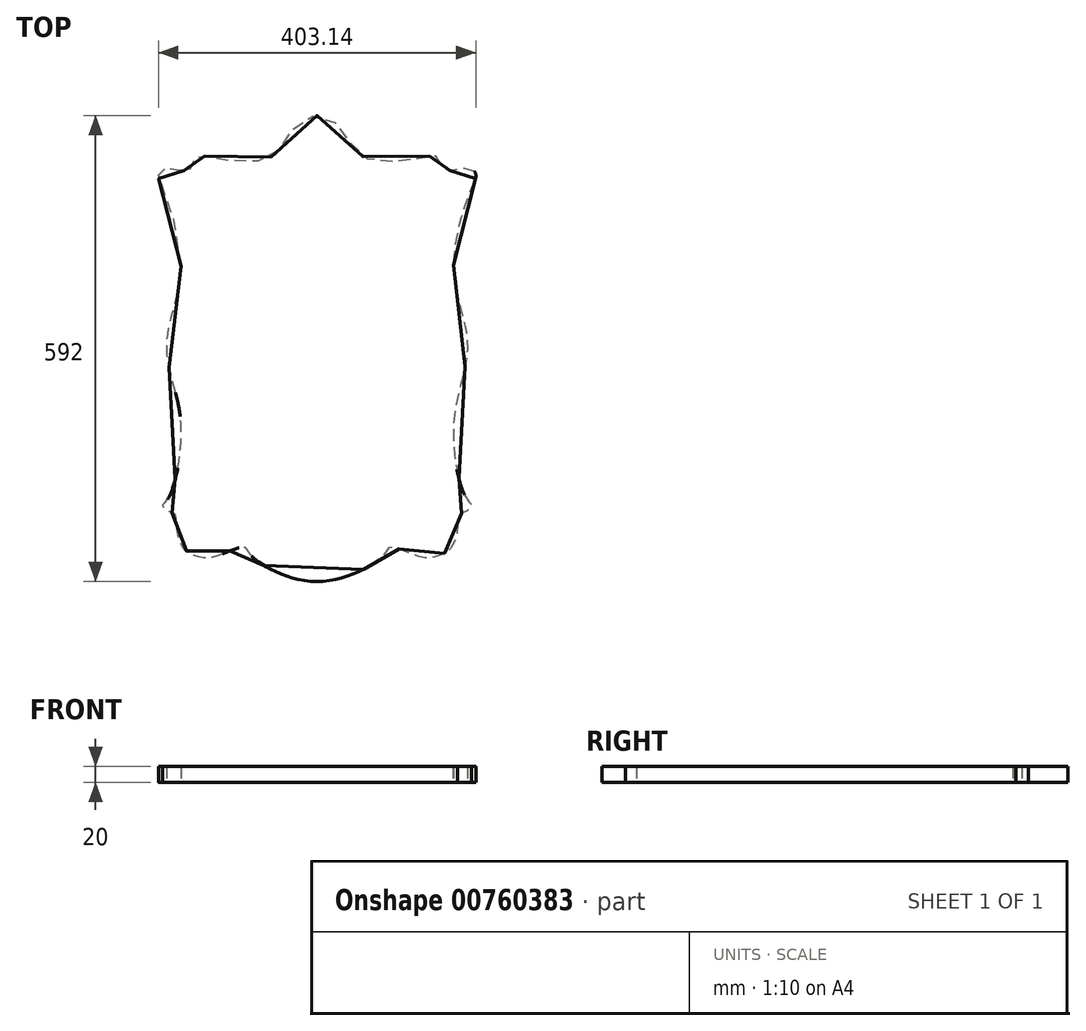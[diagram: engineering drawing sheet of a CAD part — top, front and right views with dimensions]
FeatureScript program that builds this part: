
annotation { "Feature Type Name" : "Feature", "Feature Type Description" : "" }
export const myFeature = defineFeature(function(context is Context, id is Id, definition is map)
    precondition{}
    {
        {
            var Q0;
            Q0=qCreatedBy(makeId("Top.planeOp"),FACE);
            var sketch = newSketch(context, id + "F0", { "sketchPlane" : qUnion([Q0])});
            skPoint(sketch, "E0", {"position": v(140, 240) * mm});
            skPoint(sketch, "E1", {"position": v(163, 223) * mm});
            skPoint(sketch, "E2", {"position": v(185, 225) * mm});
            skPoint(sketch, "E3", {"position": v(197, 202) * mm});
            skPoint(sketch, "E4", {"position": v(196, -202) * mm});
            skPoint(sketch, "E5", {"position": v(140, -270) * mm});
            skPoint(sketch, "E6", {"position": v(90, -258) * mm});
            skPoint(sketch, "E7", {"position": v(0, -300) * mm});
            skPoint(sketch, "E8", {"position": v(180, -216) * mm});
            skPoint(sketch, "E9", {"position": v(173, 101) * mm});
            skPoint(sketch, "E10", {"position": v(191, 0) * mm});
            skPoint(sketch, "E11", {"position": v(0, 292) * mm});
            skPoint(sketch, "E12", {"position": v(95, 234) * mm});
            skPoint(sketch, "E13", {"position": v(173, -101) * mm});
            skPoint(sketch, "E14", {"position": v(-158.4, 227.4) * mm});
            skPoint(sketch, "E15", {"position": v(-200.24, 220.68) * mm});
            skPoint(sketch, "E16", {"position": v(-169.15, 222.02) * mm});
            skPoint(sketch, "E17", {"position": v(-54.11, 242.56) * mm});
            skPoint(sketch, "E18", {"position": v(-31.45, 273.93) * mm});
            skPoint(sketch, "E19", {"position": v(-155, 238.03) * mm});
            skPoint(sketch, "E20", {"position": v(-194.35, 225.38) * mm});
            skPoint(sketch, "E21", {"position": v(-201.42, 213.06) * mm});
            skLineSegment(sketch, "E22", {"start": v(0, 292) * mm, "end": v(0, -300) * mm, "construction": true});
            skPoint(sketch, "E23.MirrorP", {"position": v(-95, 234) * mm});
            skPoint(sketch, "E24.MirrorP", {"position": v(-140, 240) * mm});
            skPoint(sketch, "E25.MirrorP", {"position": v(-163, 223) * mm});
            skPoint(sketch, "E26.MirrorP", {"position": v(-185, 225) * mm});
            skPoint(sketch, "E27.MirrorP", {"position": v(-197, 202) * mm});
            skPoint(sketch, "E28.MirrorP", {"position": v(-173, 101) * mm});
            skPoint(sketch, "E29.MirrorP", {"position": v(-191, 0) * mm});
            skPoint(sketch, "E30.MirrorP", {"position": v(-173, -101) * mm});
            skPoint(sketch, "E31.MirrorP", {"position": v(-196, -202) * mm});
            skPoint(sketch, "E32.MirrorP", {"position": v(-180, -216) * mm});
            skPoint(sketch, "E33.MirrorP", {"position": v(-140, -270) * mm});
            skPoint(sketch, "E34.MirrorP", {"position": v(-90, -258) * mm});
            skPoint(sketch, "E35", {"position": v(0, 0) * mm});
            skPoint(sketch, "E36", {"position": v(-190.7, -196.69) * mm});
            skPoint(sketch, "E37", {"position": v(-178.47, -230.66) * mm});
            skPoint(sketch, "E38", {"position": v(-190.7, -210) * mm});
            skPoint(sketch, "E39", {"position": v(-170.86, -255.98) * mm});
            skPoint(sketch, "E40", {"position": v(-123.63, -266.12) * mm});
            skPoint(sketch, "E41", {"position": v(-79, -271.56) * mm});
            skPoint(sketch, "E42", {"position": v(-87.69, -261.38) * mm});
            skPoint(sketch, "E43", {"position": v(-94.51, -256.16) * mm});
            skPoint(sketch, "E44", {"position": v(-155.65, -266.93) * mm});
            skPoint(sketch, "E45", {"position": v(-195.44, -204.34) * mm});
            skPoint(sketch, "E46.MirrorP", {"position": v(79, -271.56) * mm});
            skPoint(sketch, "E47.MirrorP", {"position": v(87.69, -261.38) * mm});
            skPoint(sketch, "E48.MirrorP", {"position": v(94.51, -256.16) * mm});
            skPoint(sketch, "E49.MirrorP", {"position": v(123.64, -266.11) * mm});
            skPoint(sketch, "E50.MirrorP", {"position": v(155.65, -266.93) * mm});
            skPoint(sketch, "E51.MirrorP", {"position": v(178.47, -230.66) * mm});
            skPoint(sketch, "E52.MirrorP", {"position": v(190.7, -210) * mm});
            skPoint(sketch, "E53.MirrorP", {"position": v(195.44, -204.34) * mm});
            skPoint(sketch, "E54.MirrorP", {"position": v(190.7, -196.69) * mm});
            skPoint(sketch, "E55.MirrorP", {"position": v(201.42, 213.06) * mm});
            skPoint(sketch, "E56.MirrorP", {"position": v(200.24, 220.68) * mm});
            skPoint(sketch, "E57.MirrorP", {"position": v(194.35, 225.38) * mm});
            skPoint(sketch, "E58.MirrorP", {"position": v(169.14, 222.03) * mm});
            skPoint(sketch, "E59.MirrorP", {"position": v(158.4, 227.4) * mm});
            skPoint(sketch, "E60.MirrorP", {"position": v(155, 238.03) * mm});
            skPoint(sketch, "E61.MirrorP", {"position": v(54.11, 242.56) * mm});
            skPoint(sketch, "E62.MirrorP", {"position": v(31.45, 273.93) * mm});
            skPoint(sketch, "E63", {"position": v(-182.2, -213.64) * mm});
            skPoint(sketch, "E64", {"position": v(-147.51, 241.77) * mm});
            skPoint(sketch, "E65.MirrorP", {"position": v(170.86, -255.98) * mm});
            skPoint(sketch, "E66.MirrorP", {"position": v(147.51, 241.77) * mm});
            skFitSpline(sketch, "E67", {"points": [v(-173, 101) * mm, v(-197, 202) * mm, v(-201.42, 213.06) * mm, v(-200.24, 220.68) * mm, v(-194.35, 225.38) * mm, v(-185, 225) * mm, v(-169.15, 222.02) * mm, v(-163, 223) * mm, v(-158.4, 227.4) * mm, v(-155, 238.03) * mm, v(-147.51, 241.77) * mm, v(-140, 240) * mm, v(-95, 234) * mm, v(-54.11, 242.56) * mm, v(-31.45, 273.93) * mm, v(0, 292) * mm, v(31.45, 273.93) * mm, v(54.11, 242.56) * mm, v(95, 234) * mm, v(140, 240) * mm, v(147.51, 241.77) * mm, v(155, 238.03) * mm, v(158.4, 227.4) * mm, v(163, 223) * mm, v(169.15, 222.03) * mm, v(185, 225) * mm, v(194.35, 225.38) * mm, v(200.24, 220.68) * mm, v(201.42, 213.06) * mm, v(197, 202) * mm, v(173, 101) * mm, v(191, 0) * mm, v(173, -101) * mm, v(190.7, -196.69) * mm, v(196, -202) * mm, v(195.44, -204.34) * mm, v(190.7, -210) * mm, v(180, -216) * mm, v(178.47, -230.66) * mm, v(170.86, -255.98) * mm, v(155.65, -266.93) * mm, v(140, -270) * mm, v(123.64, -266.11) * mm, v(94.51, -256.16) * mm, v(90, -258) * mm, v(87.69, -261.38) * mm, v(79, -271.56) * mm, v(0, -300) * mm, v(-79, -271.56) * mm, v(-87.69, -261.38) * mm, v(-90, -258) * mm, v(-94.51, -256.16) * mm, v(-123.63, -266.12) * mm, v(-140, -270) * mm, v(-155.65, -266.93) * mm, v(-170.86, -255.98) * mm, v(-178.47, -230.66) * mm, v(-180, -216) * mm, v(-182.2, -213.64) * mm, v(-190.7, -210) * mm, v(-195.44, -204.34) * mm, v(-196, -202) * mm, v(-190.7, -196.69) * mm, v(-173, -101) * mm, v(-191, 0) * mm, v(-173, 101) * mm]});
            skSolve(sketch);
        }
        {
            var Q0;
            Q0=makeQuery(id+"F0.imprint","IMPRINT",FACE,{"disambiguationData":[TD([[makeQuery(id+"F0.imprint","IMPRINT",EDGE,{"derivedFrom":sQuery(id+"F0.wireOp",EDGE,"E67")}),-1.0]])]});
            extrude(context, id + "F1", {"entities" : qUnion([Q0]), "depth" : 20 * mm});
        }
    });
